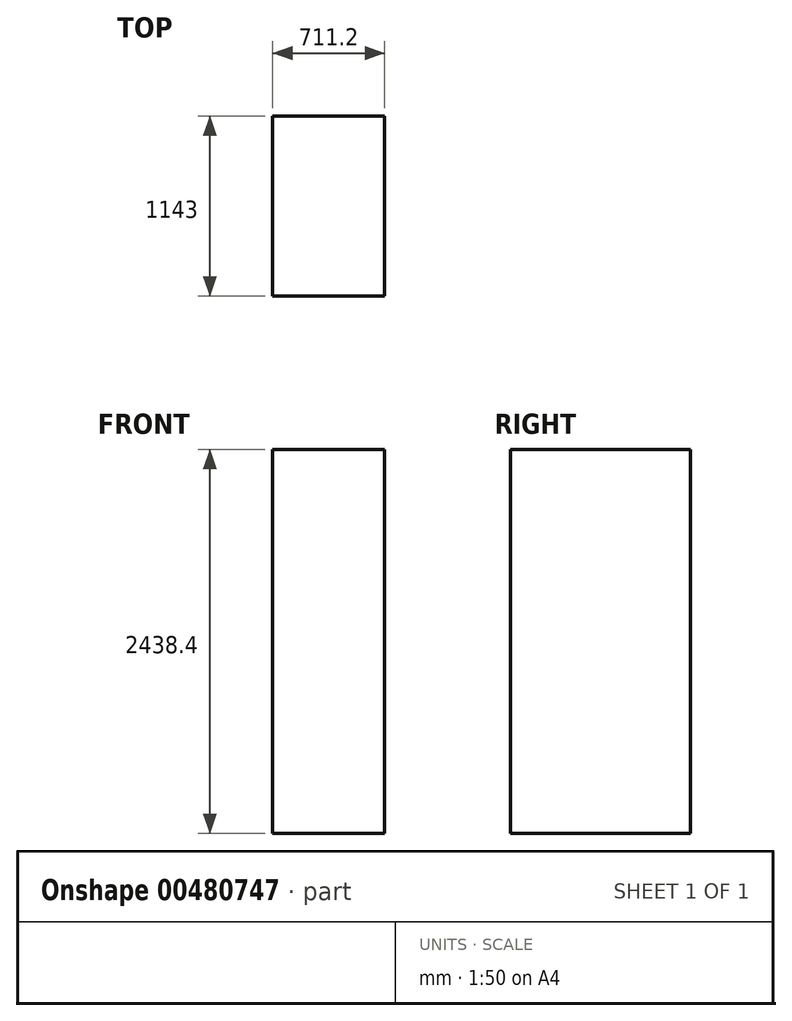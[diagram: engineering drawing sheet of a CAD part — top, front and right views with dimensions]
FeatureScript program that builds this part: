
annotation { "Feature Type Name" : "Feature", "Feature Type Description" : "" }
export const myFeature = defineFeature(function(context is Context, id is Id, definition is map)
    precondition{}
    {
        {
            var Q0;
            Q0=qCreatedBy(makeId("Top.planeOp"),FACE);
            var sketch = newSketch(context, id + "F0", { "sketchPlane" : qUnion([Q0])});
            skLineSegment(sketch, "E0.bottom", {"start": v(355.6, 571.5) * mm, "end": v(-355.6, 571.5) * mm});
            skLineSegment(sketch, "E0.top", {"start": v(355.6, -571.5) * mm, "end": v(-355.6, -571.5) * mm});
            skLineSegment(sketch, "E0.left", {"start": v(355.6, 571.5) * mm, "end": v(355.6, -571.5) * mm});
            skLineSegment(sketch, "E0.right", {"start": v(-355.6, 571.5) * mm, "end": v(-355.6, -571.5) * mm});
            skPoint(sketch, "E0.middle", {"position": v(0, 0) * mm});
            skSolve(sketch);
        }
        {
            var Q0;
            Q0=makeQuery(id+"F0.imprint","IMPRINT",FACE,{"disambiguationData":[TD([[makeQuery(id+"F0.imprint","IMPRINT",EDGE,{"derivedFrom":sQuery(id+"F0.wireOp",EDGE,"E0.bottom")}),1.0]])]});
            extrude(context, id + "F1", {"entities" : qUnion([Q0]), "depth" : 2438.4 * mm});
        }
    });
